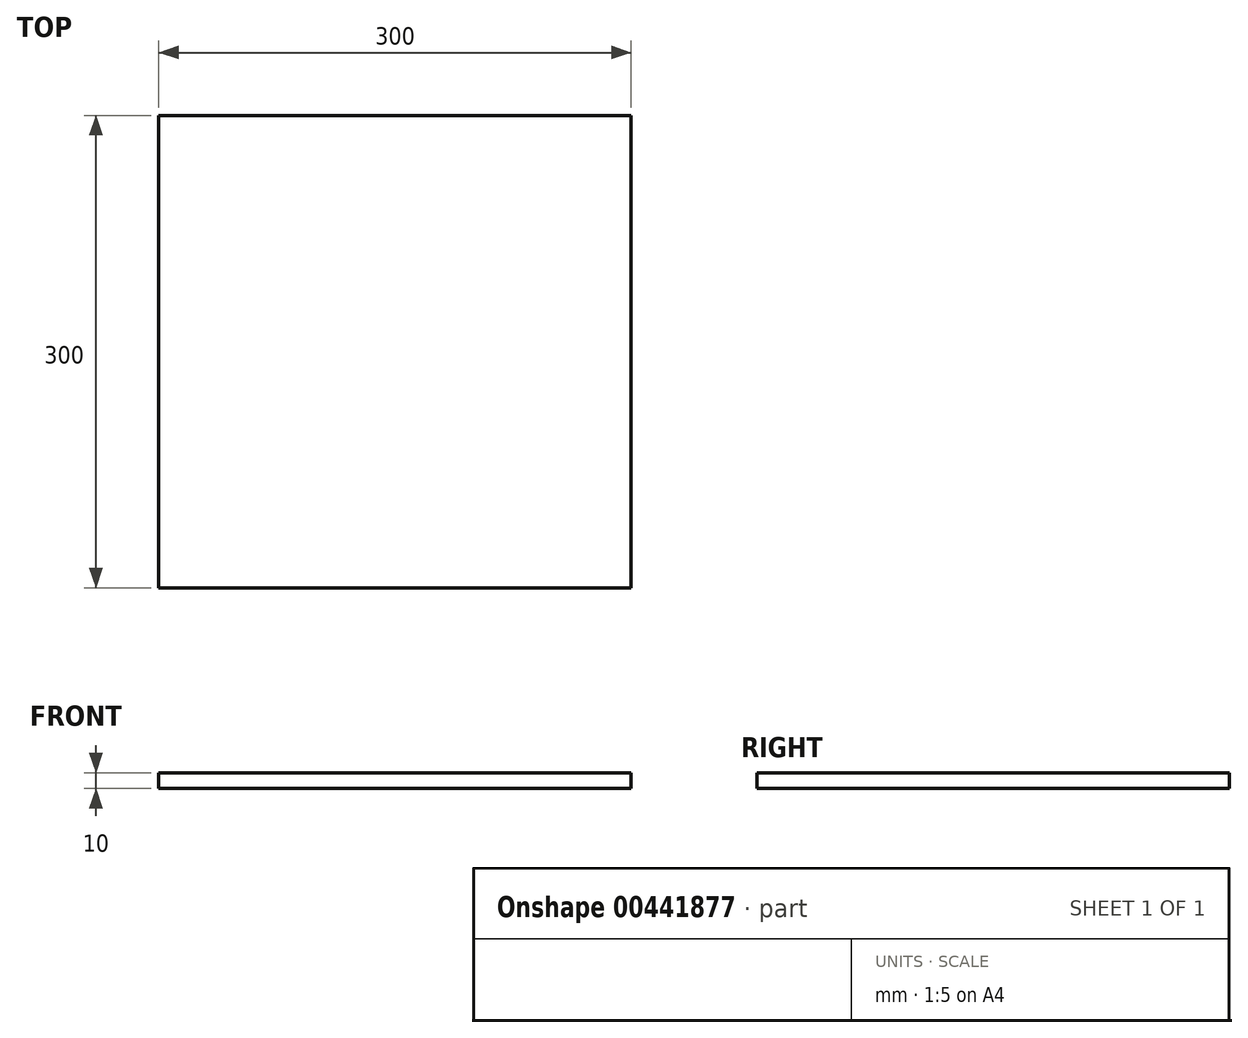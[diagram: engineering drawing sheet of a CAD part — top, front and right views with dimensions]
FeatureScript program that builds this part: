
annotation { "Feature Type Name" : "Feature", "Feature Type Description" : "" }
export const myFeature = defineFeature(function(context is Context, id is Id, definition is map)
    precondition{}
    {
        {
            var Q0;
            Q0=qCreatedBy(makeId("Top.planeOp"),FACE);
            var sketch = newSketch(context, id + "F0", { "sketchPlane" : qUnion([Q0])});
            skLineSegment(sketch, "E0.bottom", {"start": v(150, -150) * mm, "end": v(-150, -150) * mm});
            skLineSegment(sketch, "E0.top", {"start": v(150, 150) * mm, "end": v(-150, 150) * mm});
            skLineSegment(sketch, "E0.left", {"start": v(150, -150) * mm, "end": v(150, 150) * mm});
            skLineSegment(sketch, "E0.right", {"start": v(-150, -150) * mm, "end": v(-150, 150) * mm});
            skPoint(sketch, "E0.middle", {"position": v(0, 0) * mm});
            skSolve(sketch);
        }
        {
            var Q0;
            Q0 = qSketchRegion(id + "F0", true);
            extrude(context, id + "F1", {"entities" : qUnion([Q0]), "depth" : 10 * mm});
        }
    });
